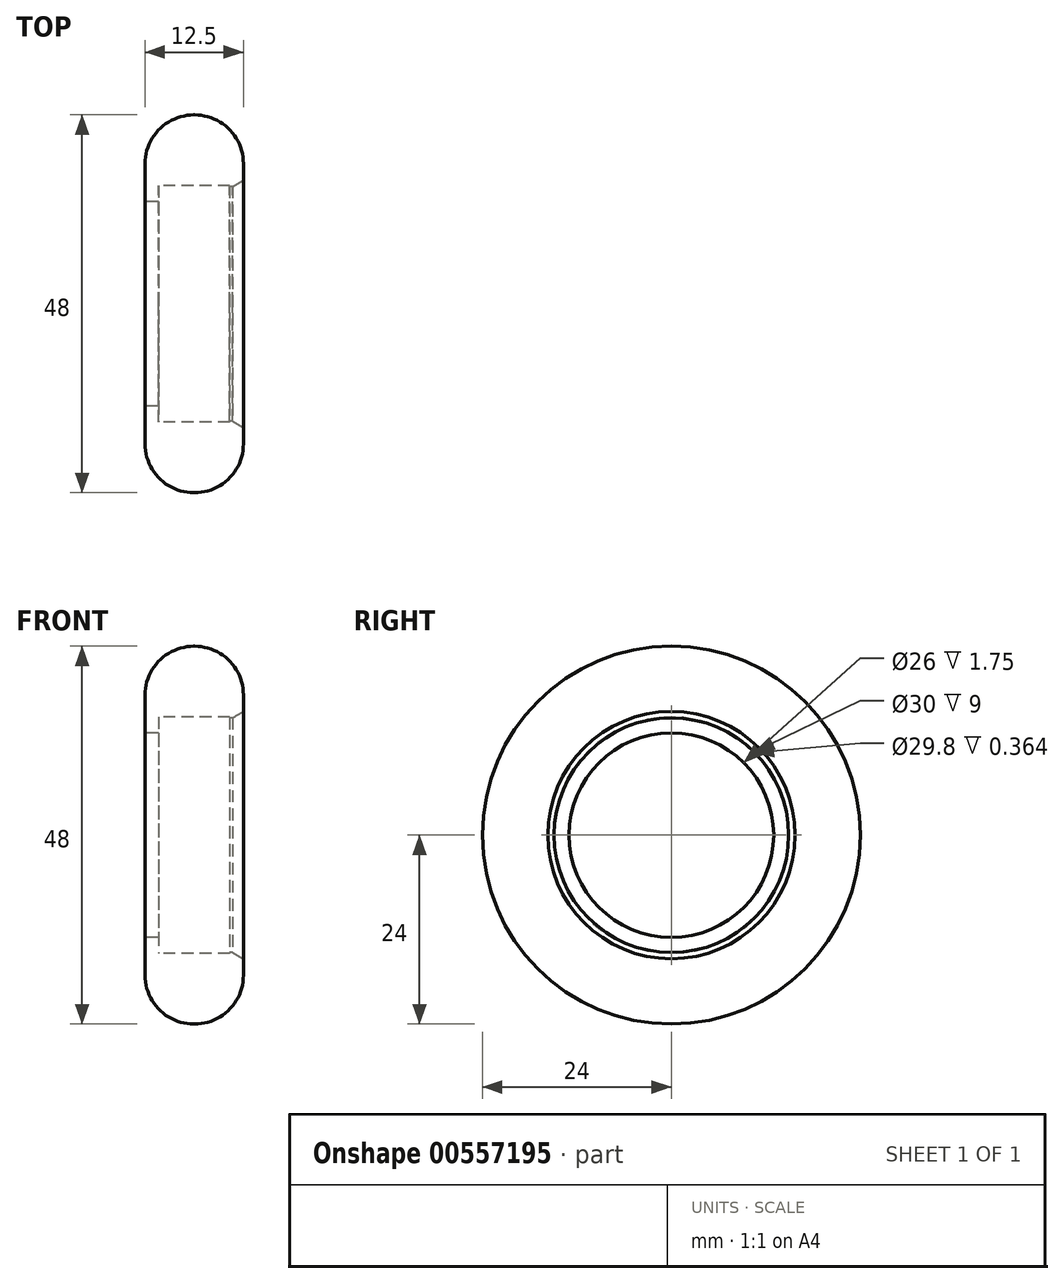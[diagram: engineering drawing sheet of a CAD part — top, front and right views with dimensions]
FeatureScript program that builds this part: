
annotation { "Feature Type Name" : "Feature", "Feature Type Description" : "" }
export const myFeature = defineFeature(function(context is Context, id is Id, definition is map)
    precondition{}
    {
        {
            var Q0;
            Q0=qCreatedBy(makeId("Front.planeOp"),FACE);
            var sketch = newSketch(context, id + "F0", { "sketchPlane" : qUnion([Q0])});
            skLineSegment(sketch, "E0.top", {"start": v(6.2, 24) * mm, "end": v(6.3, 24) * mm});
            skLineSegment(sketch, "E0.left", {"start": v(0, 13) * mm, "end": v(0, 17.8) * mm});
            skLineSegment(sketch, "E1", {"start": v(0, 13) * mm, "end": v(1.75, 13) * mm});
            skLineSegment(sketch, "E2", {"start": v(1.75, 13) * mm, "end": v(1.75, 15) * mm});
            skLineSegment(sketch, "E3", {"start": v(1.75, 15) * mm, "end": v(10.75, 15) * mm});
            skLineSegment(sketch, "E4", {"start": v(10.75, 15) * mm, "end": v(10.75, 14.9) * mm});
            skLineSegment(sketch, "E5", {"start": v(10.75, 14.9) * mm, "end": v(12.5, 14.9) * mm});
            skLineSegment(sketch, "E6", {"start": v(12.5, 14.9) * mm, "end": v(12.5, 17.8) * mm});
            skPoint(sketch, "E7.visualSharp", {"position": v(0, 24) * mm});
            skArc(sketch, "E7.filletArc", {"start": v(6.2, 24) * mm, "mid": v(1.82, 22.18) * mm, "end": v(0, 17.8) * mm});
            skPoint(sketch, "E8.visualSharp", {"position": v(12.5, 24) * mm});
            skArc(sketch, "E8.filletArc", {"start": v(12.5, 17.8) * mm, "mid": v(10.68, 22.18) * mm, "end": v(6.3, 24) * mm});
            skLineSegment(sketch, "E9", {"start": v(0, 0) * mm, "end": v(32.37, 0) * mm, "construction": true});
            skSolve(sketch);
        }
        {
            var Q0;
            Q0=makeQuery(id+"F0.imprint","IMPRINT",FACE,{"disambiguationData":[TD([[makeQuery(id+"F0.imprint","IMPRINT",EDGE,{"derivedFrom":sQuery(id+"F0.wireOp",EDGE,"E0.left")}),-1.0]])]});
            var Q1;
            Q1=sQuery(id+"F0.wireOp",EDGE,"E9");
            revolve(context, id + "F1", {"entities" : qUnion([Q0]), "axis" : qUnion([Q1]), "revolveType" : RevolveType.FULL});
        }
        {
            var Q0;
            Q0=makeQuery(id+"F1.opRevolve","SWEPT_EDGE",EDGE,{"disambiguationData":[OSD([sQuery(id+"F0.wireOp",EDGE,"E5"),sQuery(id+"F0.wireOp",EDGE,"E6")])]});
            chamfer(context, id + "F2", {"entities" : qUnion([Q0]), "chamferType" : ChamferType.OFFSET_ANGLE, "width" : 0.8 * mm, "oppositeDirection" : false, "angle" : 60 * degree, "tangentPropagation" : true});
        }
    });
